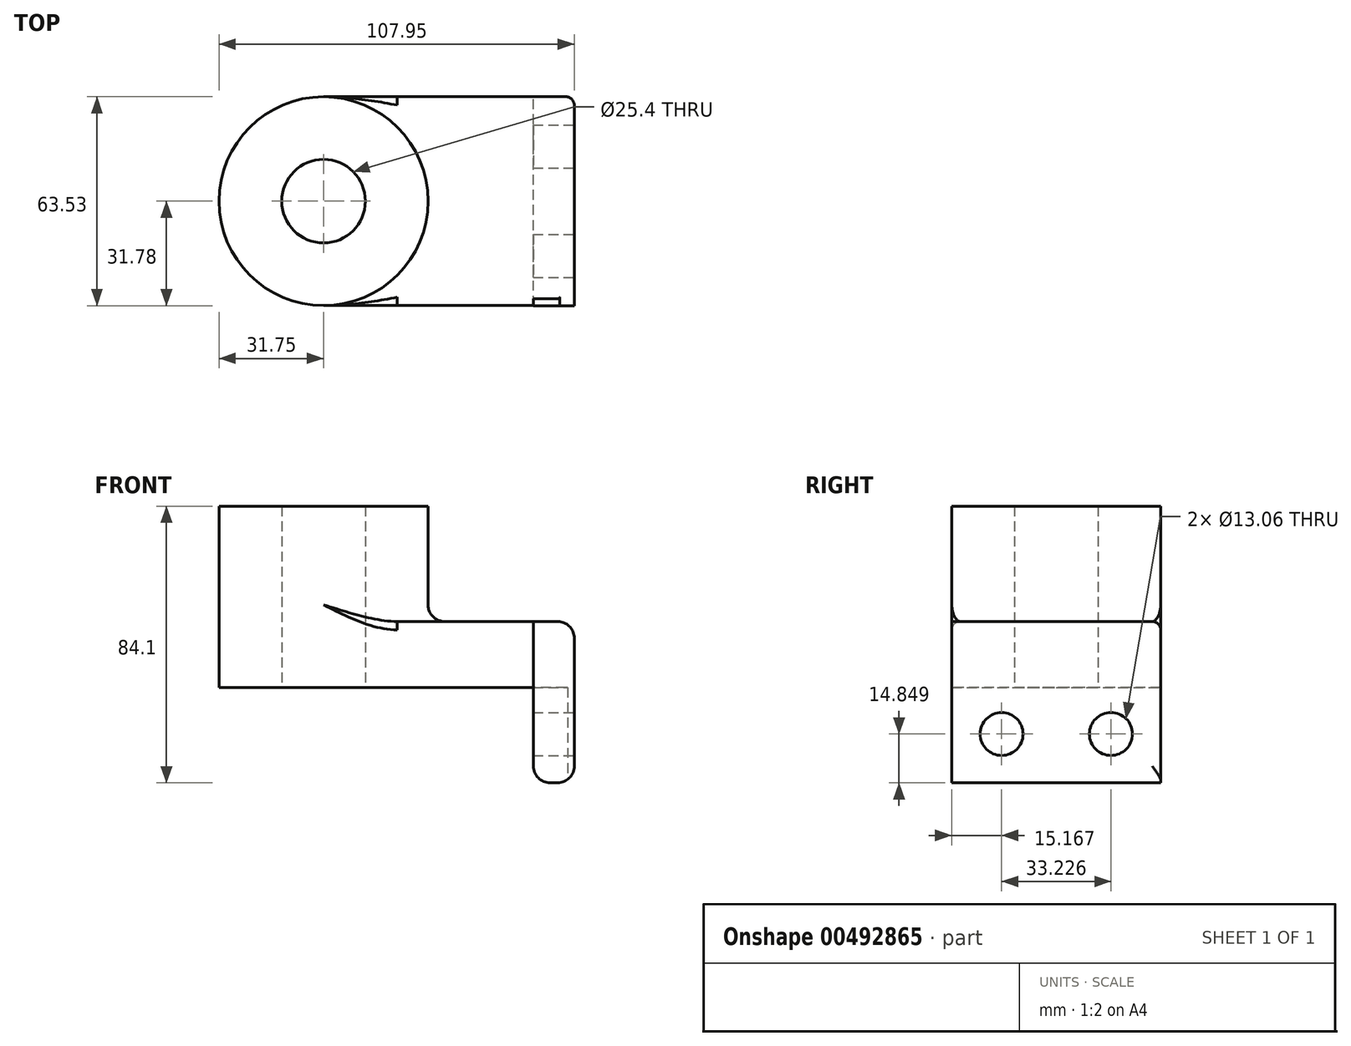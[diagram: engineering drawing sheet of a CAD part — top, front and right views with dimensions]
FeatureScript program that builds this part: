
annotation { "Feature Type Name" : "Feature", "Feature Type Description" : "" }
export const myFeature = defineFeature(function(context is Context, id is Id, definition is map)
    precondition{}
    {
        {
            var Q0;
            Q0=qCreatedBy(makeId("Top.planeOp"),FACE);
            var sketch = newSketch(context, id + "F0", { "sketchPlane" : qUnion([Q0])});
            skLineSegment(sketch, "E0.bottom", {"start": v(38.1, -31.75) * mm, "end": v(-38.1, -31.75) * mm});
            skLineSegment(sketch, "E0.top", {"start": v(38.1, 31.75) * mm, "end": v(-38.1, 31.75) * mm});
            skLineSegment(sketch, "E0.left", {"start": v(38.1, -31.75) * mm, "end": v(38.1, 31.75) * mm});
            skLineSegment(sketch, "E0.right", {"start": v(-38.1, -31.75) * mm, "end": v(-38.1, 31.75) * mm});
            skPoint(sketch, "E0.middle", {"position": v(0, 0) * mm});
            skCircle(sketch, "E1", {"center": v(-38.1, 0) * mm, "radius": 31.75 * mm});
            skCircle(sketch, "E2", {"center": v(-38.1, 0) * mm, "radius": 12.7 * mm});
            skSolve(sketch);
        }
        {
            var Q0;
            Q0 = qSketchRegion(id + "F0", true);
            extrude(context, id + "F1", {"entities" : qUnion([Q0]), "depth" : 20.07 * mm});
        }
        {
            var Q0;
            {var subQ1=sQuery(id+"F0.wireOp",EDGE,"E0.right");var subQ3=sQuery(id+"F0.wireOp",EDGE,"E2");var subQ4=makeQuery(id+"F0.imprint","INTERSECT",VERTEX,{"disambiguationData":[OD(0.0)],"derivedFrom":[subQ1,subQ3]});Q0=makeQuery(id+"F0.imprint","IMPRINT",FACE,{"disambiguationData":[TD([[makeQuery(id+"F0.imprint","IMPRINT",EDGE,{"disambiguationData":[TD([[subQ4,-1.0]])],"derivedFrom":subQ3}),-1.0]])]});}
            var Q1;
            {var subQ1=sQuery(id+"F0.wireOp",EDGE,"E0.right");var subQ3=sQuery(id+"F0.wireOp",EDGE,"E2");var subQ4=makeQuery(id+"F0.imprint","INTERSECT",VERTEX,{"disambiguationData":[OD(0.0)],"derivedFrom":[subQ1,subQ3]});Q1=makeQuery(id+"F0.imprint","IMPRINT",FACE,{"disambiguationData":[TD([[makeQuery(id+"F0.imprint","IMPRINT",EDGE,{"disambiguationData":[TD([[subQ4,1.0]])],"derivedFrom":subQ3}),-1.0]])]});}
            extrude(context, id + "F2", {"entities" : qUnion([Q0, Q1]), "operationType" : NewBodyOperationType.ADD, "depth" : 55.12 * mm});
        }
        {
            var Q0;
            Q0=makeQuery(id+"F1.opExtrude","SWEPT_FACE",FACE,{"disambiguationData":[OSD([sQuery(id+"F0.wireOp",EDGE,"E0.left")])]});
            var sketch = newSketch(context, id + "F3", { "sketchPlane" : qUnion([Q0])});
            skSolve(sketch);
        }
        {
            var Q0;
            {var subQ0=sQuery(id+"F0.wireOp",EDGE,"E0.left");Q0=makeQuery(id+"F3.imprint","IMPRINT",FACE,{"disambiguationData":[TD([[makeQuery(id+"F3.imprint","IMPRINT",EDGE,{"derivedFrom":makeQuery(id+"F1.opExtrude","CAP_EDGE",EDGE,{"disambiguationData":[OSD([subQ0])],"isStart":true})}),1.0]])]});}
            var sketch = newSketch(context, id + "F4", { "sketchPlane" : qUnion([Q0])});
            skLineSegment(sketch, "E3.bottom", {"start": v(-31.78, 20.03) * mm, "end": v(31.69, 20.03) * mm});
            skLineSegment(sketch, "E3.top", {"start": v(-31.78, -28.98) * mm, "end": v(31.69, -28.98) * mm});
            skLineSegment(sketch, "E3.left", {"start": v(-31.78, 20.03) * mm, "end": v(-31.78, -28.98) * mm});
            skLineSegment(sketch, "E3.right", {"start": v(31.69, 20.03) * mm, "end": v(31.69, -28.98) * mm});
            skCircle(sketch, "E4", {"center": v(-16.61, -14.13) * mm, "radius": 6.53 * mm});
            skCircle(sketch, "E5.MirrorC", {"center": v(16.61, -14.13) * mm, "radius": 6.53 * mm});
            skSolve(sketch);
        }
        {
            var Q0;
            {var subQ1=sQuery(id+"F4.wireOp",EDGE,"E3.top");Q0=makeQuery(id+"F4.imprint","IMPRINT",FACE,{"disambiguationData":[TD([[makeQuery(id+"F4.imprint","IMPRINT",EDGE,{"derivedFrom":subQ1}),1.0]])]});}
            var Q1;
            {var subQ0=sQuery(id+"F4.wireOp",EDGE,"E3.right");var subQ1=sQuery(id+"F4.wireOp",EDGE,"E3.bottom");var subQ2=makeQuery(id+"F4.imprint","INTERSECT",VERTEX,{"derivedFrom":[subQ1,subQ0]});Q1=makeQuery(id+"F4.imprint","IMPRINT",FACE,{"disambiguationData":[TD([[makeQuery(id+"F4.imprint","IMPRINT",EDGE,{"disambiguationData":[TD([[subQ2,-1.0]])],"derivedFrom":subQ0}),-1.0]])]});}
            extrude(context, id + "F5", {"entities" : qUnion([Q0, Q1]), "operationType" : NewBodyOperationType.ADD, "oppositeDirection" : true, "depth" : 12.45 * mm});
        }
        {
            var Q0;
            Q0=makeQuery(id+"F1.opExtrude","CAP_EDGE",EDGE,{"disambiguationData":[OSD([sQuery(id+"F0.wireOp",EDGE,"E0.left")])],"isStart":false});
            var Q1;
            {var subQ0=sQuery(id+"F0.wireOp",EDGE,"E1");Q1=makeQuery(id+"F2.boolean.opBoolean","INTERSECT",EDGE,{"derivedFrom":[makeQuery(id+"F1.opExtrude","CAP_FACE",FACE,{"disambiguationData":[OSD([sQuery(id+"F0.wireOp",EDGE,"E0.bottom"),sQuery(id+"F0.wireOp",EDGE,"E0.top"),sQuery(id+"F0.wireOp",EDGE,"E0.left"),subQ0,sQuery(id+"F0.wireOp",EDGE,"E2")])],"isStart":false}),makeQuery(id+"F2.opExtrude","SWEPT_FACE",FACE,{"disambiguationData":[OSD([subQ0])]})]});}
            var Q2;
            Q2=makeQuery(id+"F5.opExtrude","CAP_EDGE",EDGE,{"disambiguationData":[OSD([sQuery(id+"F4.wireOp",EDGE,"E3.top")])],"isStart":true});
            var Q3;
            Q3=makeQuery(id+"F5.opExtrude","CAP_EDGE",EDGE,{"disambiguationData":[OSD([sQuery(id+"F4.wireOp",EDGE,"E3.top")])],"isStart":false});
            fillet(context, id + "F6", {"entities" : qUnion([Q0, Q1, Q2, Q3]), "radius" : 5.08 * mm, "tangentPropagation" : true, "allowEdgeOverflow" : false});
        }
        {
            var Q0;
            Q0=makeQuery(id+"F1.opExtrude","CAP_EDGE",EDGE,{"disambiguationData":[OSD([sQuery(id+"F0.wireOp",EDGE,"E0.bottom")])],"isStart":false});
            var Q1;
            Q1=makeQuery(id+"F1.opExtrude","CAP_EDGE",EDGE,{"disambiguationData":[OSD([sQuery(id+"F0.wireOp",EDGE,"E0.top")])],"isStart":false});
            fillet(context, id + "F7", {"entities" : qUnion([Q0, Q1]), "radius" : 2.54 * mm, "tangentPropagation" : true, "allowEdgeOverflow" : false});
        }
    });
